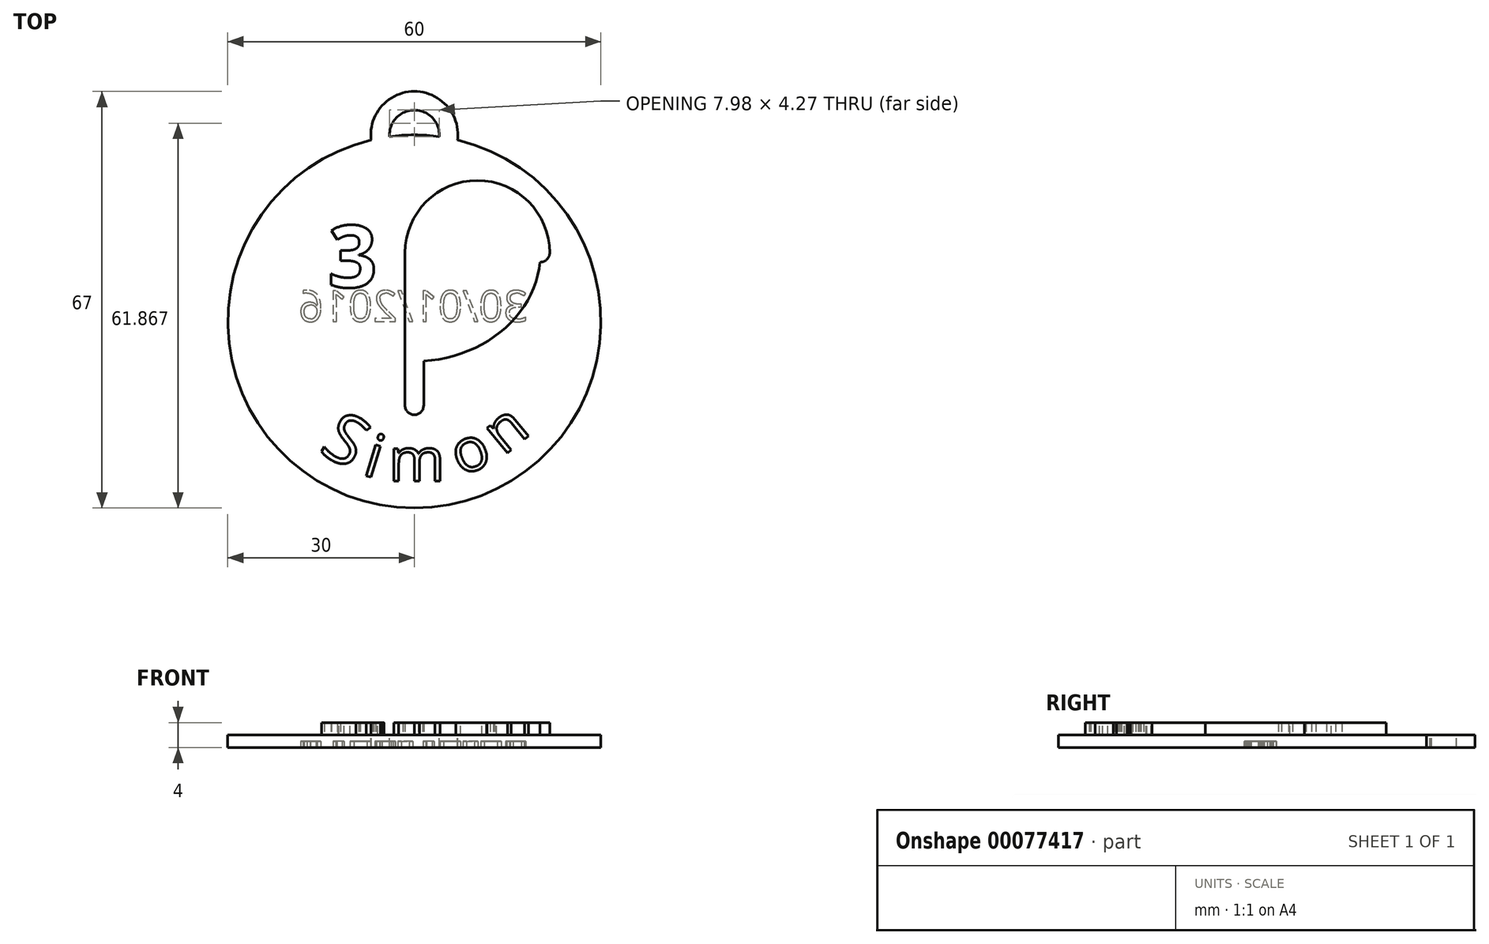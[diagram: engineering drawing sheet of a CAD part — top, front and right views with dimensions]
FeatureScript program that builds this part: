
annotation { "Feature Type Name" : "Feature", "Feature Type Description" : "" }
export const myFeature = defineFeature(function(context is Context, id is Id, definition is map)
    precondition{}
    {
        {
            var Q0;
            Q0=qCreatedBy(makeId("Top.planeOp"),FACE);
            var sketch = newSketch(context, id + "F0", { "sketchPlane" : qUnion([Q0])});
            skCircle(sketch, "E0", {"center": v(0, 0) * mm, "radius": 30 * mm});
            skSolve(sketch);
        }
        {
            var Q0;
            Q0=qSketchRegion(id+"F0",true);
            extrude(context, id + "F1", {"entities" : qUnion([Q0]), "oppositeDirection" : true, "depth" : 2 * mm});
        }
        {
            var Q0;
            Q0=qCreatedBy(makeId("Top.planeOp"),FACE);
            var sketch = newSketch(context, id + "F2", { "sketchPlane" : qUnion([Q0])});
            skEllipticalArc(sketch, "E1", {});
            skLineSegment(sketch, "E2", {"start": v(0, 0) * mm, "end": v(0, 30) * mm, "construction": true});
            skLineSegment(sketch, "E3", {"start": v(0, 11.04) * mm, "end": v(0, -13.5) * mm});
            skArc(sketch, "E4", {"start": v(20.27, 11.04) * mm, "mid": v(10.13, 21.17) * mm, "end": v(0, 11.04) * mm});
            skLineSegment(sketch, "E5", {"start": v(0, 11.04) * mm, "end": v(-16.84, 20.76) * mm, "construction": true});
            skLineSegment(sketch, "E6", {"start": v(0, 11.04) * mm, "end": v(-20.27, 11.04) * mm, "construction": true});
            skArc(sketch, "E7.0.startCap", {"start": v(-1.5, 11.04) * mm, "mid": v(0, 12.54) * mm, "end": v(1.5, 11.04) * mm});
            skArc(sketch, "E7.0.endCap", {"start": v(1.5, -13.5) * mm, "mid": v(0, -15) * mm, "end": v(-1.5, -13.5) * mm});
            skLineSegment(sketch, "E7.0.left", {"start": v(1.5, 11.04) * mm, "end": v(1.5, -13.5) * mm});
            skLineSegment(sketch, "E7.0.right", {"start": v(-1.5, 11.04) * mm, "end": v(-1.5, -13.5) * mm});
            skArc(sketch, "E8.0.startCap", {"start": v(21.77, 11.04) * mm, "mid": v(20.27, 9.54) * mm, "end": v(18.77, 11.04) * mm});
            skArc(sketch, "E8.0.endCap", {"start": v(1.5, 11.04) * mm, "mid": v(0, 9.54) * mm, "end": v(-1.5, 11.04) * mm});
            skArc(sketch, "E8.0.left", {"start": v(18.77, 11.04) * mm, "mid": v(10.13, 19.67) * mm, "end": v(1.5, 11.04) * mm});
            skArc(sketch, "E8.0.right", {"start": v(21.77, 11.04) * mm, "mid": v(10.13, 22.67) * mm, "end": v(-1.5, 11.04) * mm});
            skArc(sketch, "E8.1.startCap", {"start": v(-18.02, 21.68) * mm, "mid": v(-15.91, 21.95) * mm, "end": v(-15.65, 19.84) * mm});
            skArc(sketch, "E8.1.endCap", {"start": v(18.77, 11.04) * mm, "mid": v(20.27, 12.54) * mm, "end": v(21.77, 11.04) * mm});
            skFitSpline(sketch, "E8.1.left", {"points": [v(18.7, 9.5) * mm, v(18.8, 11.04) * mm, v(18.7, 12.6) * mm, v(18.36, 14.63) * mm, v(17.66, 16.6) * mm, v(16.63, 18.49) * mm, v(15.37, 20.3) * mm, v(13.44, 22.32) * mm, v(11.07, 24) * mm, v(8.94, 25.1) * mm, v(6.7, 26.01) * mm, v(4.32, 26.63) * mm, v(1.87, 26.95) * mm, v(0, 27.03) * mm, v(-1.87, 26.95) * mm, v(-4.32, 26.63) * mm, v(-6.7, 26.01) * mm, v(-8.94, 25.1) * mm, v(-11.07, 24) * mm, v(-13.44, 22.32) * mm, v(-15.37, 20.3) * mm, v(-16.63, 18.49) * mm, v(-17.66, 16.6) * mm, v(-18.36, 14.63) * mm, v(-18.7, 12.6) * mm, v(-18.8, 11.04) * mm, v(-18.7, 9.5) * mm, v(-18.36, 7.46) * mm, v(-17.66, 5.48) * mm, v(-16.63, 3.6) * mm, v(-15.37, 1.8) * mm, v(-13.44, -0.24) * mm, v(-11.07, -1.92) * mm, v(-8.94, -3.02) * mm, v(-6.7, -3.93) * mm, v(-4.32, -4.55) * mm, v(-1.87, -4.86) * mm, v(0, -4.94) * mm, v(1.87, -4.86) * mm, v(4.32, -4.55) * mm, v(6.7, -3.93) * mm, v(8.94, -3.02) * mm, v(11.07, -1.92) * mm, v(13.44, -0.24) * mm, v(15.37, 1.8) * mm, v(16.63, 3.6) * mm, v(17.66, 5.48) * mm, v(18.36, 7.46) * mm, v(18.7, 9.5) * mm, v(18.8, 11.04) * mm, v(18.7, 12.6) * mm]});
            skFitSpline(sketch, "E8.1.right", {"points": [v(21.7, 9.15) * mm, v(21.8, 11.04) * mm, v(21.7, 12.93) * mm, v(21.27, 15.42) * mm, v(20.42, 17.81) * mm, v(19.18, 20.07) * mm, v(17.69, 22.22) * mm, v(15.4, 24.61) * mm, v(12.65, 26.56) * mm, v(10.2, 27.83) * mm, v(7.62, 28.88) * mm, v(4.92, 29.58) * mm, v(2.12, 29.94) * mm, v(0, 30.03) * mm, v(-2.12, 29.94) * mm, v(-4.92, 29.58) * mm, v(-7.62, 28.88) * mm, v(-10.2, 27.83) * mm, v(-12.65, 26.56) * mm, v(-15.4, 24.61) * mm, v(-17.69, 22.22) * mm, v(-19.18, 20.07) * mm, v(-20.42, 17.81) * mm, v(-21.27, 15.42) * mm, v(-21.7, 12.93) * mm, v(-21.8, 11.04) * mm, v(-21.7, 9.15) * mm, v(-21.27, 6.67) * mm, v(-20.42, 4.27) * mm, v(-19.18, 2) * mm, v(-17.69, -0.14) * mm, v(-15.4, -2.53) * mm, v(-12.65, -4.48) * mm, v(-10.2, -5.75) * mm, v(-7.62, -6.8) * mm, v(-4.92, -7.5) * mm, v(-2.12, -7.86) * mm, v(0, -7.95) * mm, v(2.12, -7.86) * mm, v(4.92, -7.5) * mm, v(7.62, -6.8) * mm, v(10.2, -5.75) * mm, v(12.65, -4.48) * mm, v(15.4, -2.53) * mm, v(17.69, -0.14) * mm, v(19.18, 2) * mm, v(20.42, 4.27) * mm, v(21.27, 6.67) * mm, v(21.7, 9.15) * mm, v(21.8, 11.04) * mm, v(21.7, 12.93) * mm]});
            const initialGuessF2  = {"E1": [0, 0.011041626236194823, 1, 0, 0.020266667008310185, 0.017458373763805178, 2.5511335140588507, 0]};
            skSetInitialGuess(sketch, initialGuessF2);
            skSolve(sketch);
        }
        {
            var Q0;
            {var subQ0=sQuery(id+"F2.wireOp",EDGE,"E8.1.startCap");Q0=makeQuery(id+"F2.imprint","IMPRINT",FACE,{"disambiguationData":[TD([[makeQuery(id+"F2.imprint","IMPRINT",EDGE,{"derivedFrom":subQ0}),-1.0]])]});}
            var Q1;
            {var subQ0=sQuery(id+"F2.wireOp",EDGE,"E7.0.right");var subQ1=sQuery(id+"F2.wireOp",EDGE,"E1");var subQ2=makeQuery(id+"F2.imprint","INTERSECT",VERTEX,{"derivedFrom":[subQ1,subQ0]});Q1=makeQuery(id+"F2.imprint","IMPRINT",FACE,{"disambiguationData":[TD([[makeQuery(id+"F2.imprint","IMPRINT",EDGE,{"disambiguationData":[TD([[subQ2,-1.0]])],"derivedFrom":subQ1}),1.0]])]});}
            var Q2;
            {var subQ0=sQuery(id+"F2.wireOp",EDGE,"E3");var subQ1=sQuery(id+"F2.wireOp",EDGE,"E1");var subQ2=makeQuery(id+"F2.imprint","INTERSECT",VERTEX,{"derivedFrom":[subQ1,subQ0]});Q2=makeQuery(id+"F2.imprint","IMPRINT",FACE,{"disambiguationData":[TD([[makeQuery(id+"F2.imprint","IMPRINT",EDGE,{"disambiguationData":[TD([[subQ2,-1.0]])],"derivedFrom":subQ1}),1.0]])]});}
            var Q3;
            {var subQ0=sQuery(id+"F2.wireOp",EDGE,"E7.0.right");var subQ1=sQuery(id+"F2.wireOp",EDGE,"E1");var subQ2=makeQuery(id+"F2.imprint","INTERSECT",VERTEX,{"derivedFrom":[subQ1,subQ0]});Q3=makeQuery(id+"F2.imprint","IMPRINT",FACE,{"disambiguationData":[TD([[makeQuery(id+"F2.imprint","IMPRINT",EDGE,{"disambiguationData":[TD([[subQ2,-1.0]])],"derivedFrom":subQ1}),-1.0]])]});}
            var Q4;
            {var subQ0=sQuery(id+"F2.wireOp",EDGE,"E3");var subQ1=sQuery(id+"F2.wireOp",EDGE,"E1");var subQ2=makeQuery(id+"F2.imprint","INTERSECT",VERTEX,{"derivedFrom":[subQ1,subQ0]});Q4=makeQuery(id+"F2.imprint","IMPRINT",FACE,{"disambiguationData":[TD([[makeQuery(id+"F2.imprint","IMPRINT",EDGE,{"disambiguationData":[TD([[subQ2,-1.0]])],"derivedFrom":subQ1}),-1.0]])]});}
            var Q5;
            {var subQ0=sQuery(id+"F2.wireOp",EDGE,"E7.0.left");var subQ1=sQuery(id+"F2.wireOp",EDGE,"E1");var subQ2=makeQuery(id+"F2.imprint","INTERSECT",VERTEX,{"derivedFrom":[subQ1,subQ0]});Q5=makeQuery(id+"F2.imprint","IMPRINT",FACE,{"disambiguationData":[TD([[makeQuery(id+"F2.imprint","IMPRINT",EDGE,{"disambiguationData":[TD([[subQ2,-1.0]])],"derivedFrom":subQ1}),-1.0]])]});}
            var Q6;
            {var subQ0=sQuery(id+"F2.wireOp",EDGE,"E7.0.left");var subQ1=sQuery(id+"F2.wireOp",EDGE,"E1");var subQ2=makeQuery(id+"F2.imprint","INTERSECT",VERTEX,{"derivedFrom":[subQ1,subQ0]});Q6=makeQuery(id+"F2.imprint","IMPRINT",FACE,{"disambiguationData":[TD([[makeQuery(id+"F2.imprint","IMPRINT",EDGE,{"disambiguationData":[TD([[subQ2,-1.0]])],"derivedFrom":subQ1}),1.0]])]});}
            var Q7;
            {var subQ0=sQuery(id+"F2.wireOp",EDGE,"E4");var subQ1=sQuery(id+"F2.wireOp",EDGE,"E1");var subQ2=makeQuery(id+"F2.imprint","INTERSECT",VERTEX,{"derivedFrom":[subQ1,subQ0]});Q7=makeQuery(id+"F2.imprint","IMPRINT",FACE,{"disambiguationData":[TD([[makeQuery(id+"F2.imprint","IMPRINT",EDGE,{"disambiguationData":[TD([[subQ2,1.0]])],"derivedFrom":subQ1}),-1.0]])]});}
            var Q8;
            {var subQ0=sQuery(id+"F2.wireOp",EDGE,"E4");var subQ1=sQuery(id+"F2.wireOp",EDGE,"E1");var subQ2=makeQuery(id+"F2.imprint","INTERSECT",VERTEX,{"derivedFrom":[subQ1,subQ0]});Q8=makeQuery(id+"F2.imprint","IMPRINT",FACE,{"disambiguationData":[TD([[makeQuery(id+"F2.imprint","IMPRINT",EDGE,{"disambiguationData":[TD([[subQ2,1.0]])],"derivedFrom":subQ1}),1.0]])]});}
            var Q9;
            {var subQ5=sQuery(id+"F2.wireOp",EDGE,"E8.0.left");Q9=makeQuery(id+"F2.imprint","IMPRINT",FACE,{"disambiguationData":[TD([[makeQuery(id+"F2.imprint","IMPRINT",EDGE,{"derivedFrom":subQ5}),-1.0]])]});}
            var Q10;
            {var subQ5=sQuery(id+"F2.wireOp",EDGE,"E8.0.right");Q10=makeQuery(id+"F2.imprint","IMPRINT",FACE,{"disambiguationData":[TD([[makeQuery(id+"F2.imprint","IMPRINT",EDGE,{"derivedFrom":subQ5}),1.0]])]});}
            var Q11;
            {var subQ0=sQuery(id+"F2.wireOp",EDGE,"E4");var subQ1=sQuery(id+"F2.wireOp",EDGE,"E3");var subQ2=makeQuery(id+"F2.imprint","INTERSECT",VERTEX,{"derivedFrom":[subQ1,subQ0]});Q11=makeQuery(id+"F2.imprint","IMPRINT",FACE,{"disambiguationData":[TD([[makeQuery(id+"F2.imprint","IMPRINT",EDGE,{"disambiguationData":[TD([[subQ2,-1.0]])],"derivedFrom":subQ1}),-1.0]])]});}
            var Q12;
            {var subQ0=sQuery(id+"F2.wireOp",EDGE,"E4");var subQ1=sQuery(id+"F2.wireOp",EDGE,"E3");var subQ2=makeQuery(id+"F2.imprint","INTERSECT",VERTEX,{"derivedFrom":[subQ1,subQ0]});Q12=makeQuery(id+"F2.imprint","IMPRINT",FACE,{"disambiguationData":[TD([[makeQuery(id+"F2.imprint","IMPRINT",EDGE,{"disambiguationData":[TD([[subQ2,-1.0]])],"derivedFrom":subQ1}),1.0]])]});}
            var Q13;
            {var subQ0=sQuery(id+"F2.wireOp",EDGE,"E8.0.endCap");var subQ1=sQuery(id+"F2.wireOp",EDGE,"E3");var subQ2=makeQuery(id+"F2.imprint","INTERSECT",VERTEX,{"derivedFrom":[subQ1,subQ0]});Q13=makeQuery(id+"F2.imprint","IMPRINT",FACE,{"disambiguationData":[TD([[makeQuery(id+"F2.imprint","IMPRINT",EDGE,{"disambiguationData":[TD([[subQ2,-1.0]])],"derivedFrom":subQ1}),-1.0]])]});}
            var Q14;
            {var subQ0=sQuery(id+"F2.wireOp",EDGE,"E8.0.endCap");var subQ1=sQuery(id+"F2.wireOp",EDGE,"E3");var subQ2=makeQuery(id+"F2.imprint","INTERSECT",VERTEX,{"derivedFrom":[subQ1,subQ0]});Q14=makeQuery(id+"F2.imprint","IMPRINT",FACE,{"disambiguationData":[TD([[makeQuery(id+"F2.imprint","IMPRINT",EDGE,{"disambiguationData":[TD([[subQ2,-1.0]])],"derivedFrom":subQ1}),1.0]])]});}
            var Q15;
            {var subQ1=sQuery(id+"F2.wireOp",EDGE,"E7.0.endCap");Q15=makeQuery(id+"F2.imprint","IMPRINT",FACE,{"disambiguationData":[TD([[makeQuery(id+"F2.imprint","IMPRINT",EDGE,{"derivedFrom":subQ1}),-1.0]])]});}
            extrude(context, id + "F3", {"entities" : qUnion([Q0, Q1, Q2, Q3, Q4, Q5, Q6, Q7, Q8, Q9, Q10, Q11, Q12, Q13, Q14, Q15]), "operationType" : NewBodyOperationType.ADD, "depth" : 2 * mm});
        }
        {
            var Q0;
            Q0=qCreatedBy(makeId("Top.planeOp"),FACE);
            var sketch = newSketch(context, id + "F4", { "sketchPlane" : qUnion([Q0])});
            skText(sketch, "E9", { "text": "3", "fontName": "OpenSans-Bold.ttf"});
            skText(sketch, "E10", { "text": "D", "fontName": "OpenSans-Bold.ttf"});
            const initialGuessF4  = {"E9": [-0.0139, 0.0055, 1, 0, 0.01], "E10": [0.0055, 0.0055, 1, 0, 0.01]};
            skSetInitialGuess(sketch, initialGuessF4);
            skSolve(sketch);
        }
        {
            var Q0;
            Q0=qSketchRegion(id+"F4",true);
            extrude(context, id + "F5", {"entities" : qUnion([Q0]), "operationType" : NewBodyOperationType.ADD, "depth" : 2 * mm});
        }
        {
            var Q0;
            {var subQ8=sQuery(id+"F0.wireOp",EDGE,"E0");Q0=makeQuery(id+"F3.boolean.opBoolean","SPLIT",FACE,{"disambiguationData":[TD([makeQuery(id+"F1.opExtrude","SWEPT_FACE",FACE,{"disambiguationData":[OSD([subQ8])]})])],"derivedFrom":makeQuery(id+"F1.opExtrude","CAP_FACE",FACE,{"disambiguationData":[OSD([subQ8])],"isStart":true})});}
            var sketch = newSketch(context, id + "F6", { "sketchPlane" : qUnion([Q0])});
            skCircle(sketch, "E11.0", {"center": v(0, 0) * mm, "radius": 26 * mm, "construction": true});
            skText(sketch, "E12", { "text": "S", "fontName": "OpenSans-Regular.ttf"});
            skText(sketch, "E13", { "text": "i", "fontName": "OpenSans-Regular.ttf"});
            skText(sketch, "E14", { "text": "m", "fontName": "OpenSans-Regular.ttf"});
            skText(sketch, "E15", { "text": "o", "fontName": "OpenSans-Regular.ttf"});
            skText(sketch, "E16", { "text": "n", "fontName": "OpenSans-Regular.ttf"});
            const initialGuessF6  = {"E12": [-0.01555, -0.02084, 0.86081, -0.50893, 0.008], "E13": [-0.00854, -0.02456, 0.95474, -0.29746, 0.007], "E14": [-0.00413, -0.02567, 1, 0, 0.007], "E15": [0.00743, -0.02492, 0.924, 0.38237, 0.007], "E16": [0.01433, -0.0217, 0.77517, 0.63175, 0.007]};
            skSetInitialGuess(sketch, initialGuessF6);
            skSolve(sketch);
        }
        {
            var Q0;
            Q0=qSketchRegion(id+"F6",true);
            extrude(context, id + "F7", {"entities" : qUnion([Q0]), "operationType" : NewBodyOperationType.ADD, "depth" : 2 * mm});
        }
        {
            var Q0;
            Q0=qCreatedBy(makeId("Top.planeOp"),FACE);
            var sketch = newSketch(context, id + "F8", { "sketchPlane" : qUnion([Q0])});
            skArc(sketch, "E17", {"start": v(5.48, 29.5) * mm, "mid": v(0, 35.5) * mm, "end": v(-5.48, 29.5) * mm});
            skArc(sketch, "E18.0.startCap", {"start": v(6.97, 29.36) * mm, "mid": v(5.34, 28) * mm, "end": v(3.98, 29.63) * mm});
            skArc(sketch, "E18.0.endCap", {"start": v(-3.98, 29.63) * mm, "mid": v(-5.34, 28) * mm, "end": v(-6.97, 29.36) * mm});
            skArc(sketch, "E18.0.left", {"start": v(3.98, 29.63) * mm, "mid": v(0, 34) * mm, "end": v(-3.98, 29.63) * mm});
            skArc(sketch, "E18.0.right", {"start": v(6.97, 29.36) * mm, "mid": v(0, 37) * mm, "end": v(-6.97, 29.36) * mm});
            skSolve(sketch);
        }
        {
            var Q0;
            Q0=qSketchRegion(id+"F8",true);
            extrude(context, id + "F9", {"entities" : qUnion([Q0]), "operationType" : NewBodyOperationType.ADD, "oppositeDirection" : true, "depth" : 2 * mm});
        }
        {
            var Q0;
            Q0=makeQuery(id+"F9.boolean.opBoolean","MERGE",FACE,{"derivedFrom":[makeQuery(id+"F1.opExtrude","CAP_FACE",FACE,{"disambiguationData":[OSD([sQuery(id+"F0.wireOp",EDGE,"E0")])],"isStart":false}),makeQuery(id+"F9.opExtrude","CAP_FACE",FACE,{"disambiguationData":[OSD([sQuery(id+"F8.wireOp",EDGE,"E18.0.startCap"),sQuery(id+"F8.wireOp",EDGE,"E18.0.endCap"),sQuery(id+"F8.wireOp",EDGE,"E18.0.left"),sQuery(id+"F8.wireOp",EDGE,"E18.0.right")])],"isStart":false})]});
            var sketch = newSketch(context, id + "F10", { "sketchPlane" : qUnion([Q0])});
            skText(sketch, "E19", { "text": "30/01/2016", "fontName": "OpenSans-Regular.ttf"});
            const initialGuessF10  = {"E19": [0.01826, 0, -1, 0, 0.005]};
            skSetInitialGuess(sketch, initialGuessF10);
            skSolve(sketch);
        }
        {
            var Q0;
            Q0=qSketchRegion(id+"F10",true);
            extrude(context, id + "F11", {"entities" : qUnion([Q0]), "operationType" : NewBodyOperationType.REMOVE, "oppositeDirection" : true, "depth" : 1 * mm});
        }
    });
